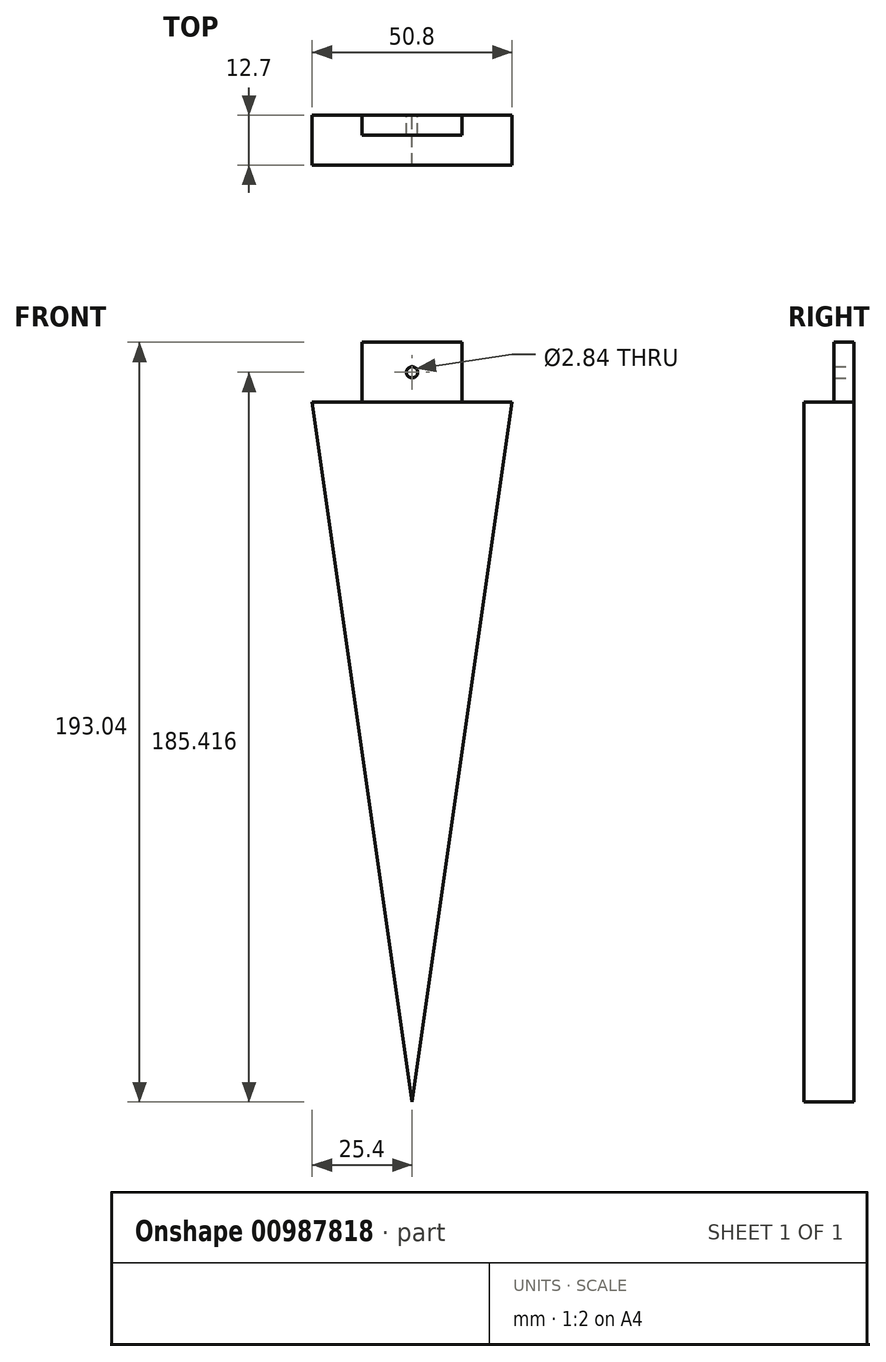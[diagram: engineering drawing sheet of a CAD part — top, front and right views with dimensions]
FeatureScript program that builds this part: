
annotation { "Feature Type Name" : "Feature", "Feature Type Description" : "" }
export const myFeature = defineFeature(function(context is Context, id is Id, definition is map)
    precondition{}
    {
        {
            var Q0;
            Q0=qCreatedBy(makeId("Front.planeOp"),FACE);
            var sketch = newSketch(context, id + "F0", { "sketchPlane" : qUnion([Q0])});
            skLineSegment(sketch, "E0", {"start": v(0, 53.42) * mm, "end": v(0, -124.38) * mm});
            skLineSegment(sketch, "E1", {"start": v(0, 53.42) * mm, "end": v(-25.4, 53.42) * mm});
            skLineSegment(sketch, "E2", {"start": v(-25.4, 53.42) * mm, "end": v(0, -124.38) * mm});
            skLineSegment(sketch, "E3.MirrorCS", {"start": v(0, 53.42) * mm, "end": v(25.4, 53.42) * mm});
            skLineSegment(sketch, "E4.MirrorCS", {"start": v(25.4, 53.42) * mm, "end": v(0, -124.38) * mm});
            skLineSegment(sketch, "E5", {"start": v(-12.7, 53.42) * mm, "end": v(-12.7, 68.66) * mm});
            skLineSegment(sketch, "E6", {"start": v(12.7, 53.42) * mm, "end": v(12.7, 68.66) * mm});
            skLineSegment(sketch, "E7", {"start": v(-12.7, 68.66) * mm, "end": v(12.7, 68.66) * mm});
            skCircle(sketch, "E8", {"center": v(0, 61.04) * mm, "radius": 1.42 * mm});
            skSolve(sketch);
        }
        {
            var Q0;
            {var subQ0=sQuery(id+"F0.wireOp",EDGE,"E0");Q0=makeQuery(id+"F0.imprint","IMPRINT",FACE,{"disambiguationData":[TD([[makeQuery(id+"F0.imprint","IMPRINT",EDGE,{"derivedFrom":subQ0}),-1.0]])]});}
            var Q1;
            {var subQ0=sQuery(id+"F0.wireOp",EDGE,"E0");Q1=makeQuery(id+"F0.imprint","IMPRINT",FACE,{"disambiguationData":[TD([[makeQuery(id+"F0.imprint","IMPRINT",EDGE,{"derivedFrom":subQ0}),1.0]])]});}
            extrude(context, id + "F1", {"entities" : qUnion([Q0, Q1]), "depth" : 12.7 * mm, "offsetDistance" : 25.4 * mm});
        }
        {
            var Q0;
            {var subQ1=sQuery(id+"F0.wireOp",EDGE,"E5");Q0=makeQuery(id+"F0.imprint","IMPRINT",FACE,{"disambiguationData":[TD([[makeQuery(id+"F0.imprint","IMPRINT",EDGE,{"derivedFrom":subQ1}),-1.0]])]});}
            extrude(context, id + "F2", {"entities" : qUnion([Q0]), "operationType" : NewBodyOperationType.ADD, "depth" : 5.08 * mm, "offsetDistance" : 25.4 * mm});
        }
    });
